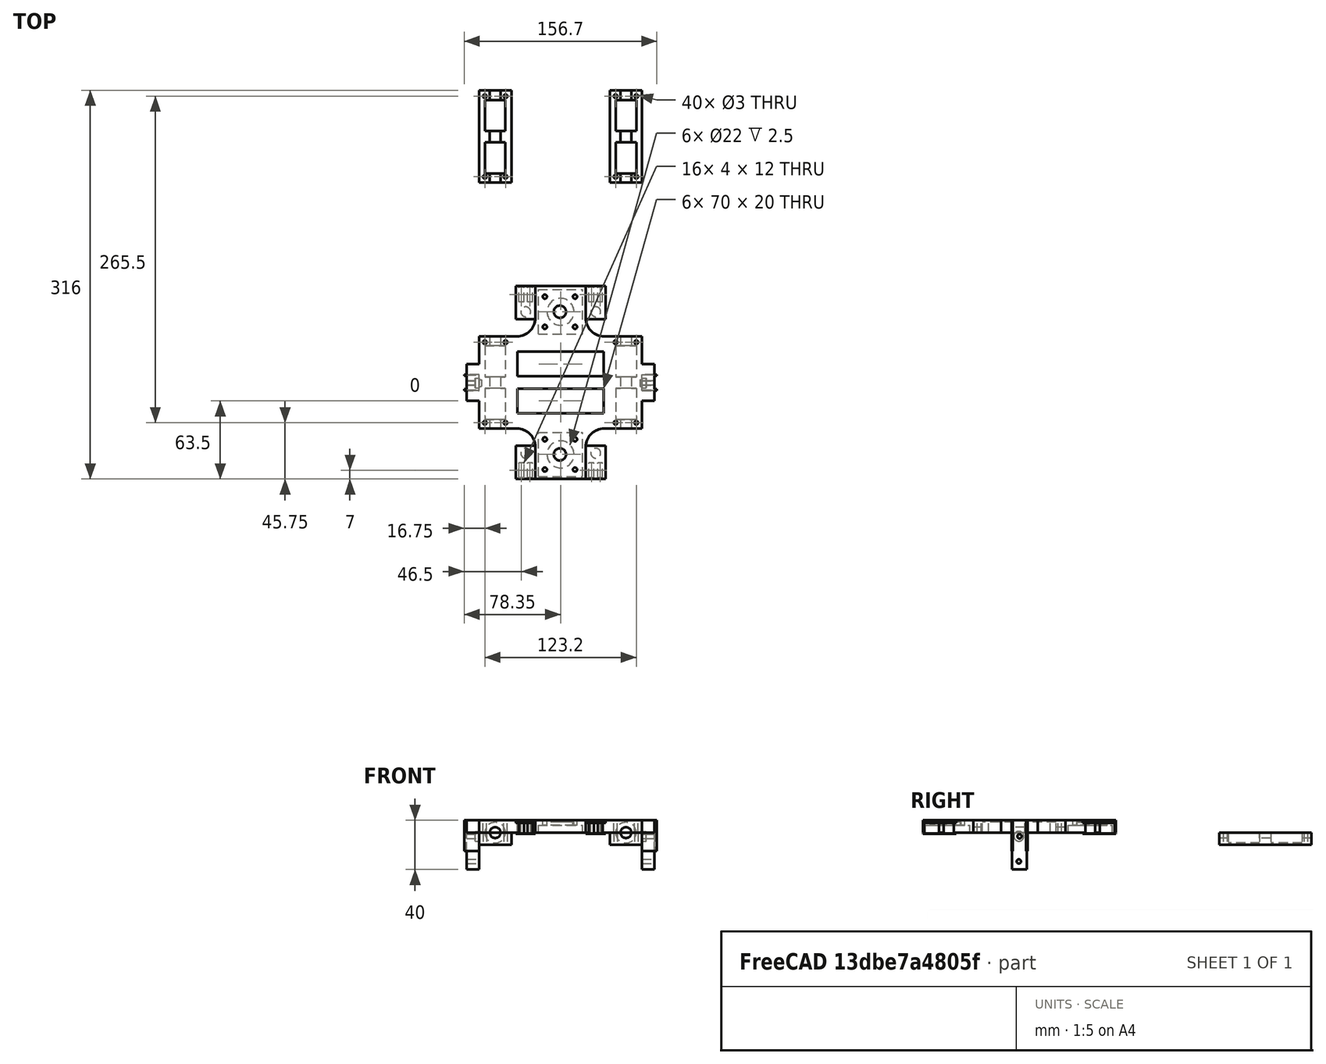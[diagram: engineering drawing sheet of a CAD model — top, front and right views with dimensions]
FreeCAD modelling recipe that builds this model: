
FCSTD DOCUMENT  (FreeCAD 0.16R6712 (Git))
Label: 1.5
License: All rights reserved
LicenseURL: http://en.wikipedia.org/wiki/All_rights_reserved
objects: Part::Cylinder×28, Part::Cut×28, Part::Box×21, Part::MultiFuse×13, Part::FeaturePython×9, Part::Fillet×4, Part::Feature×4, Part::Fuse×2
note: 109 computed .brp shape members not serialized (recipe doc carries the construction recipe); baked Part::Feature solids carry a one-line shape summary decoded from their .brp

FEATURE [Part::Box] Box  label="Cubo"
  Height = 10
  Length = 26.35
  Width = 75
FEATURE [Part::Cylinder] Cylinder  label="Cilindro"
  Angle = 360
  Height = 10
  Placement = pos=(4.75,4.75,0) rot=(0,0,1;0rad)
  Radius = 1.5
FEATURE [Part::Cylinder] Cylinder002  label="Cilindro002"
  Angle = 360
  Height = 10
  Placement = pos=(4.75,70.25,0) rot=(0,0,1;0rad)
  Radius = 1.5
FEATURE [Part::Cylinder] Cylinder003  label="Cilindro003"
  Angle = 360
  Height = 10
  Placement = pos=(21.6,4.75,0) rot=(0,0,1;0rad)
  Radius = 1.5
FEATURE [Part::Cut] Cut
  Base = -> Box
  Tool = -> Cylinder
FEATURE [Part::Cut] Cut001
  Base = -> Cut
  Tool = -> Cylinder002
FEATURE [Part::Cylinder] Cylinder004  label="Cilindro004"
  Angle = 360
  Height = 25.35
  Placement = pos=(13.175,30,0) rot=(1,0,0;1.5708rad)
  Radius = 8.4
FEATURE [Part::Cylinder] Cylinder005  label="Cilindro005"
  Angle = 360
  Height = 25.35
  Placement = pos=(13.175,64.5,0) rot=(1,0,0;1.5708rad)
  Radius = 8.4
FEATURE [Part::Cylinder] Cylinder006  label="Cilindro006"
  Angle = 360
  Height = 9.5
  Placement = pos=(13.175,39.5,0) rot=(1,0,0;1.5708rad)
  Radius = 4.4
FEATURE [Part::Fuse] Fusion
  Base = -> Cylinder004
  Tool = -> Cylinder005
FEATURE [Part::Fuse] Fusion001
  Base = -> Fusion
  Placement = pos=(0,2.75,0) rot=(0,0,1;0rad)
  Tool = -> Cylinder006
FEATURE [Part::Box] Box001  label="Centro"
  Height = 10
  Length = 80
  Placement = pos=(26.35,0,0) rot=(0,0,1;0rad)
  Width = 75
FEATURE [Part::Box] Box002  label="Lucernario"
  Height = 10
  Length = 70
  Placement = pos=(31.35,12.5,0) rot=(0,0,1;0rad)
  Width = 20
FEATURE [Part::Box] Box003  label="Lucernario2"
  Height = 10
  Length = 70
  Placement = pos=(31.35,42.5,0) rot=(0,0,1;0rad)
  Width = 20
FEATURE [Part::Cut] Cut007
  Base = -> Box001
  Tool = -> Box002
FEATURE [Part::Cut] Cut008  label="Centro1"
  Base = -> Cut007
  Tool = -> Box003
FEATURE [Part::Box] Box006  label="Guia1"
  Height = 10
  Length = 10
  Placement = pos=(-10,22.5,0) rot=(0,0,1;0rad)
  Width = 30
FEATURE [Part::Box] Box010  label="Cubo003"
  Height = 10
  Length = 26.35
  Width = 75
FEATURE [Part::Cylinder] Cylinder007  label="Cilindro007"
  Angle = 360
  Height = 25.35
  Placement = pos=(13.175,67.25,0) rot=(1,0,0;1.5708rad)
  Radius = 8.4
FEATURE [Part::Cut] Cut011
  Base = -> Box010
  Tool = -> Cylinder007
FEATURE [Part::Cylinder] Cylinder008  label="Cilindro008"
  Angle = 360
  Height = 9.5
  Placement = pos=(13.175,42.25,0) rot=(1,0,0;1.5708rad)
  Radius = 4.4
FEATURE [Part::Cut] Cut012
  Base = -> Cut011
  Tool = -> Cylinder008
FEATURE [Part::Cylinder] Cylinder009  label="Cilindro009"
  Angle = 360
  Height = 25.35
  Placement = pos=(13.175,32.75,0) rot=(1,0,0;1.5708rad)
  Radius = 8.4
FEATURE [Part::Cut] Cut013
  Base = -> Cut012
  Tool = -> Cylinder009
FEATURE [Part::Cylinder] Cylinder010  label="Cilindro010"
  Angle = 360
  Height = 10
  Placement = pos=(21.6,4.75,0) rot=(0,0,1;0rad)
  Radius = 1.5
FEATURE [Part::Cylinder] Cylinder011  label="Cilindro011"
  Angle = 360
  Height = 10
  Placement = pos=(4.75,4.75,0) rot=(0,0,1;0rad)
  Radius = 1.5
FEATURE [Part::Cut] Cut014
  Base = -> Cut013
  Tool = -> Cylinder010
FEATURE [Part::Cut] Cut015
  Base = -> Cut014
  Tool = -> Cylinder011
FEATURE [Part::Cylinder] Cylinder012  label="Cilindro012"
  Angle = 360
  Height = 10
  Placement = pos=(4.75,70.25,0) rot=(0,0,1;0rad)
  Radius = 1.5
FEATURE [Part::Cylinder] Cylinder013  label="Cilindro013"
  Angle = 360
  Height = 10
  Placement = pos=(21.6,70.25,0) rot=(0,0,1;0rad)
  Radius = 1.5
FEATURE [Part::Cut] Cut016
  Base = -> Cut015
  Tool = -> Cylinder012
FEATURE [Part::Cut] Cut017
  Base = -> Cut016
  Placement = pos=(0,0,0) rot=(0,1,0;3.14159rad)
  Tool = -> Cylinder013
FEATURE [Part::FeaturePython] Array001  label="Cierres"  # Draft array (typed FeaturePython)
  Angle = 360
  ArrayType = 0
  Axis = (0,0,1)
  Base = -> Cut017
  Center = (0,0,0)
  Fuse = false
  IntervalAxis = (0,0,0)
  IntervalX = (106.35,0,0)
  IntervalY = (0,1,0)
  IntervalZ = (0,0,0)
  NumberPolar = 1
  NumberX = 2
  NumberY = 1
  NumberZ = 1
  Placement = pos=(26.35,200,0) rot=(0,0,1;0rad)
FEATURE [Part::Box] Box011  label="Cubo004"
  Height = 10
  Length = 41
  Width = 41
FEATURE [Part::Cylinder] Cylinder014  label="Cilindro014"
  Angle = 360
  Height = 10
  Placement = pos=(7.7,7.7,0) rot=(0,0,1;0rad)
  Radius = 1.7
FEATURE [Part::Cylinder] Cylinder015  label="Cilindro015"
  Angle = 360
  Height = 10
  Placement = pos=(7.7,32.3,0) rot=(0,0,1;0rad)
  Radius = 1.7
FEATURE [Part::Cylinder] Cylinder016  label="Cilindro016"
  Angle = 360
  Height = 10
  Placement = pos=(32.3,7.7,0) rot=(0,0,1;0rad)
  Radius = 1.7
FEATURE [Part::Cylinder] Cylinder017  label="Cilindro017"
  Angle = 360
  Height = 10
  Placement = pos=(32.3,32.3,0) rot=(0,0,1;0rad)
  Radius = 1.7
FEATURE [Part::Cylinder] Cylinder018  label="Cilindro018"
  Angle = 360
  Height = 10
  Placement = pos=(20,20,0) rot=(0,0,1;0rad)
  Radius = 5
FEATURE [Part::Cut] Cut018
  Base = -> Box011
  Tool = -> Cylinder015
FEATURE [Part::Cut] Cut019
  Base = -> Cut018
  Tool = -> Cylinder014
FEATURE [Part::Cut] Cut020
  Base = -> Cut019
  Tool = -> Cylinder016
FEATURE [Part::Cut] Cut021
  Base = -> Cut020
  Tool = -> Cylinder017
FEATURE [Part::Cut] Cut022
  Base = -> Cut021
  Tool = -> Cylinder018
FEATURE [Part::Box] Box012  label="Cubo005"
  Height = 6
  Length = 36
  Placement = pos=(2.5,2,0) rot=(0,0,1;0rad)
  Width = 36
FEATURE [Part::Cut] Cut023
  Base = -> Cut022
  Placement = pos=(43.35,-46,0) rot=(0,0,1;0rad)
  Tool = -> Box012
FEATURE [Part::FeaturePython] Array002  # Draft array (typed FeaturePython)
  Angle = 360
  ArrayType = 0
  Axis = (0,0,1)
  Base = -> Cut023
  Center = (0,0,0)
  Fuse = false
  IntervalAxis = (0,0,0)
  IntervalX = (1,0,0)
  IntervalY = (0,116,0)
  IntervalZ = (0,0,0)
  NumberPolar = 1
  NumberX = 1
  NumberY = 2
  NumberZ = 1
  Placement = pos=(2.5,5,0) rot=(0,0,1;0rad)
FEATURE [Part::Box] Box014  label="Cubo007"
  Height = 25
  Length = 12
  Placement = pos=(132.7,31,-15) rot=(0,0,1;0rad)
  Width = 1
FEATURE [Part::Box] Box015  label="Cubo008"
  Height = 25
  Length = 12
  Placement = pos=(132.7,43,-15) rot=(0,0,1;0rad)
  Width = 1
FEATURE [Part::Box] Box016  label="Cubo009"
  Height = 30
  Length = 10
  Placement = pos=(-10,31.5,-30) rot=(0,0,1;0rad)
  Width = 12
FEATURE [Part::Box] Box017  label="Cubo010"
  Height = 25
  Length = 12
  Placement = pos=(-12,31,-15) rot=(0,0,1;0rad)
  Width = 1
FEATURE [Part::Box] Box018  label="Cubo011"
  Height = 25
  Length = 12
  Placement = pos=(-12,43,-15) rot=(0,0,1;0rad)
  Width = 1
FEATURE [Part::Cylinder] Cylinder019  label="Cilindro019"
  Angle = 360
  Height = 10
  Placement = pos=(-10,37.5,-3) rot=(0,1,0;1.5708rad)
  Radius = 1.75
FEATURE [Part::Cylinder] Cylinder020  label="Cilindro020"
  Angle = 360
  Height = 10
  Placement = pos=(-10,37,-23.5) rot=(0,1,0;1.5708rad)
  Radius = 1.75
FEATURE [Part::Cut] Cut024
  Base = -> Box016
  Tool = -> Cylinder020
FEATURE [Part::Cut] Cut025
  Base = -> Cut024
  Tool = -> Cylinder019
FEATURE [Part::FeaturePython] Array003  # Draft array (typed FeaturePython)
  Angle = 360
  ArrayType = 0
  Axis = (0,0,1)
  Base = -> Cut025
  Center = (0,0,0)
  Fuse = false
  IntervalAxis = (0,0,0)
  IntervalX = (142.7,0,0)
  IntervalY = (0,1,0)
  IntervalZ = (0,0,0)
  NumberPolar = 1
  NumberX = 2
  NumberY = 1
  NumberZ = 1
FEATURE [Part::MultiFuse] Fusion009
  Shapes = -> [Box015,Box014,Array003]
FEATURE [Part::MultiFuse] Fusion010
  Shapes = -> [Fusion009,Box018,Box017]
FEATURE [Part::Box] Box007  label="Guia2"
  Height = 10
  Length = 10
  Placement = pos=(132.7,22.5,0) rot=(0,0,1;0rad)
  Width = 30
FEATURE [Part::Cut] Cut026
  Base = -> Cut001
  Tool = -> Cylinder003
FEATURE [Part::Cylinder] Cylinder021  label="Cilindro021"
  Angle = 360
  Height = 10
  Placement = pos=(21.6,70.25,0) rot=(0,0,1;0rad)
  Radius = 1.5
FEATURE [Part::Cut] Cut027
  Base = -> Cut026
  Tool = -> Cylinder021
FEATURE [Part::Cut] Cut028
  Base = -> Cut027
  Tool = -> Fusion001
FEATURE [Part::FeaturePython] Array  # Draft array (typed FeaturePython)
  Angle = 360
  ArrayType = 0
  Axis = (0,0,1)
  Base = -> Cut028
  Center = (0,0,0)
  Fuse = false
  IntervalAxis = (0,0,0)
  IntervalX = (106.35,0,0)
  IntervalY = (0,1,0)
  IntervalZ = (0,0,0)
  NumberPolar = 1
  NumberX = 2
  NumberY = 1
  NumberZ = 1
FEATURE [Part::MultiFuse] Fusion011
  Shapes = -> [Array,Cut008]
FEATURE [Part::MultiFuse] Fusion012
  Shapes = -> [Array002,Fusion011]
FEATURE [Part::MultiFuse] Fusion013
  Shapes = -> [Fusion010,Fusion012]
FEATURE [Part::MultiFuse] Fusion014
  Shapes = -> [Box007,Fusion013]
FEATURE [Part::MultiFuse] Fusion015
  Shapes = -> [Box006,Fusion014]
FEATURE [Part::Fillet] Fillet
  Base = -> Fusion015
  Edges = 1 edges r=15: [Edge176]
FEATURE [Part::Fillet] Fillet001
  Base = -> Fillet
  Edges = 1 edges r=15: [Edge59]
FEATURE [Part::Fillet] Fillet002
  Base = -> Fillet001
  Edges = 1 edges r=15: [Edge73]
FEATURE [Part::Fillet] Fillet003
  Base = -> Fillet002
  Edges = 1 edges r=15: [Edge61]
FEATURE [Part::Cylinder] Cylinder022  label="Cilindro022"
  Angle = 360
  Height = 2.5
  Placement = pos=(66.35,-21,6) rot=(0,0,1;0rad)
  Radius = 11
FEATURE [Part::Cut] Cut029
  Base = -> Fillet003
  Tool = -> Cylinder022
FEATURE [Part::Cylinder] Cylinder023  label="Cilindro023"
  Angle = 360
  Height = 2.5
  Placement = pos=(66.35,95,6) rot=(0,0,1;0rad)
  Radius = 11
FEATURE [Part::Cut] Cut030
  Base = -> Cut029
  Tool = -> Cylinder023
FEATURE [Part::Feature] Cut030001  label="Cut031"
  shape: bbox 156.7 x 157 x 40 mm, 112 faces (baked)
FEATURE [Part::Feature] Array001001  label="Cierres001"
  shape: bbox 132.7 x 75 x 10 mm, 34 faces, 2 solids (baked)
FEATURE [Part::Cylinder] Cylinder024  label="Cilindro024"
  Angle = 360
  Height = 10
  Placement = pos=(38,-20,0) rot=(0,0,1;0rad)
  Radius = 4
FEATURE [Part::Box] Box019  label="Cubo012"
  Height = 0.2
  Length = 16
  Placement = pos=(29.85,-41,0) rot=(0,0,1;0rad)
  Width = 27
FEATURE [Part::MultiFuse] Fusion016
  Shapes = -> [Box019,Cylinder024]
FEATURE [Part::Box] Box020  label="Cubo013"
  Height = 10
  Length = 4
  Placement = pos=(32.5,-40,0) rot=(0,0,1;0rad)
  Width = 12
FEATURE [Part::Box] Box021  label="Cubo014"
  Height = 10
  Length = 4
  Placement = pos=(39.5,-40,0) rot=(0,0,1;0rad)
  Width = 12
FEATURE [Part::MultiFuse] Fusion017  label="Enganche"
  Shapes = -> [Box021,Box020,Fusion016]
FEATURE [Part::FeaturePython] Array001002  # Draft array (typed FeaturePython)
  Angle = 360
  ArrayType = 0
  Axis = (0,0,1)
  Base = -> Fusion017
  Center = (0,0,0)
  Fuse = false
  IntervalAxis = (0,0,0)
  IntervalX = (57,0,0)
  IntervalY = (0,1,0)
  IntervalZ = (0,0,0)
  NumberPolar = 1
  NumberX = 2
  NumberY = 1
  NumberZ = 1
  Placement = pos=(0,0,-1) rot=(0,0,1;0rad)
FEATURE [Part::Box] Box022  label="Cubo015"
  Height = 0.2
  Length = 16
  Placement = pos=(29.85,89,0) rot=(0,0,1;0rad)
  Width = 27
FEATURE [Part::Cylinder] Cylinder025  label="Cilindro025"
  Angle = 360
  Height = 10
  Placement = pos=(38,95,0) rot=(0,0,1;0rad)
  Radius = 4
FEATURE [Part::MultiFuse] Fusion018
  Shapes = -> [Cylinder025,Box022]
FEATURE [Part::Box] Box023  label="Cubo016"
  Height = 10
  Length = 4
  Placement = pos=(32.5,103,0) rot=(0,0,1;0rad)
  Width = 12
FEATURE [Part::Box] Box024  label="Cubo017"
  Height = 10
  Length = 4
  Placement = pos=(39.5,103,0) rot=(0,0,1;0rad)
  Width = 12
FEATURE [Part::MultiFuse] Fusion019
  Shapes = -> [Box023,Fusion018,Box024]
FEATURE [Part::FeaturePython] Array001003  # Draft array (typed FeaturePython)
  Angle = 360
  ArrayType = 0
  Axis = (0,0,1)
  Base = -> Fusion019
  Center = (0,0,0)
  Fuse = false
  IntervalAxis = (0,0,0)
  IntervalX = (57,0,0)
  IntervalY = (0,1,0)
  IntervalZ = (0,0,0)
  NumberPolar = 1
  NumberX = 2
  NumberY = 1
  NumberZ = 1
  Placement = pos=(0,0,-1) rot=(0,0,1;0rad)
FEATURE [Part::MultiFuse] Fusion020
  Shapes = -> [Cut030001,Array001003,Array001002]
FEATURE [Part::Box] Box025  label="Cubo018"
  Height = 2
  Length = 16
  Placement = pos=(29.85,89,9) rot=(0,0,1;0rad)
  Width = 27
FEATURE [Part::FeaturePython] Array001004  # Draft array (typed FeaturePython)
  Angle = 360
  ArrayType = 0
  Axis = (0,0,1)
  Base = -> Box025
  Center = (0,0,0)
  Fuse = false
  IntervalAxis = (0,0,0)
  IntervalX = (57,0,0)
  IntervalY = (0,1,0)
  IntervalZ = (0,0,0)
  NumberPolar = 1
  NumberX = 2
  NumberY = 1
  NumberZ = 1
FEATURE [Part::FeaturePython] Array001005  # Draft array (typed FeaturePython)
  Angle = 360
  ArrayType = 0
  Axis = (0,0,1)
  Base = -> Array001004
  Center = (0,0,0)
  Fuse = false
  IntervalAxis = (0,0,0)
  IntervalX = (1,0,0)
  IntervalY = (0,-130,0)
  IntervalZ = (0,0,0)
  NumberPolar = 1
  NumberX = 1
  NumberY = 2
  NumberZ = 1
  Placement = pos=(0,0,-1) rot=(0,0,1;0rad)
FEATURE [Part::Cylinder] Cylinder026  label="Cilindro026"
  Angle = 360
  Height = 300
  Placement = pos=(13.18,290,0) rot=(1,0,0;1.5708rad)
  Radius = 4.4
FEATURE [Part::FeaturePython] Array001006  # Draft array (typed FeaturePython)
  Angle = 360
  ArrayType = 0
  Axis = (0,0,1)
  Base = -> Cylinder026
  Center = (0,0,0)
  Fuse = false
  IntervalAxis = (0,0,0)
  IntervalX = (106.35,1,0)
  IntervalY = (0,1,0)
  IntervalZ = (0,0,0)
  NumberPolar = 1
  NumberX = 2
  NumberY = 1
  NumberZ = 1
FEATURE [Part::Cut] Cut030003
  Base = -> Array001001
  Tool = -> Array001006
FEATURE [Part::Feature] Cut030003001  label="Cut030004"
  shape: bbox 132.7 x 75 x 10 mm, 42 faces, 2 solids (baked)
FEATURE [Part::MultiFuse] Fusion021
  Shapes = -> [Array001005,Fusion020]
FEATURE [Part::Cut] Cut030003002
  Base = -> Fusion021
  Tool = -> Array001006
FEATURE [Part::Feature] Cut030003002001  label="Cut030003003"
  shape: bbox 156.7 x 157 x 40 mm, 192 faces (baked)
FEATURE [Part::Cylinder] Cylinder027  label="Cilindro027"
  Angle = 360
  Height = 5
  Placement = pos=(-3,37,-3) rot=(0,1,0;1.5708rad)
  Radius = 4
FEATURE [Part::Cut] Cut030003002002
  Base = -> Cut030003002001
  Tool = -> Cylinder027
FEATURE [Part::Cylinder] Cylinder028  label="Cilindro028"
  Angle = 360
  Height = 5
  Placement = pos=(131,37,-3) rot=(0,1,0;1.5708rad)
  Radius = 4
FEATURE [Part::Cut] Cut030003002003
  Base = -> Cut030003002002
  Tool = -> Cylinder028
